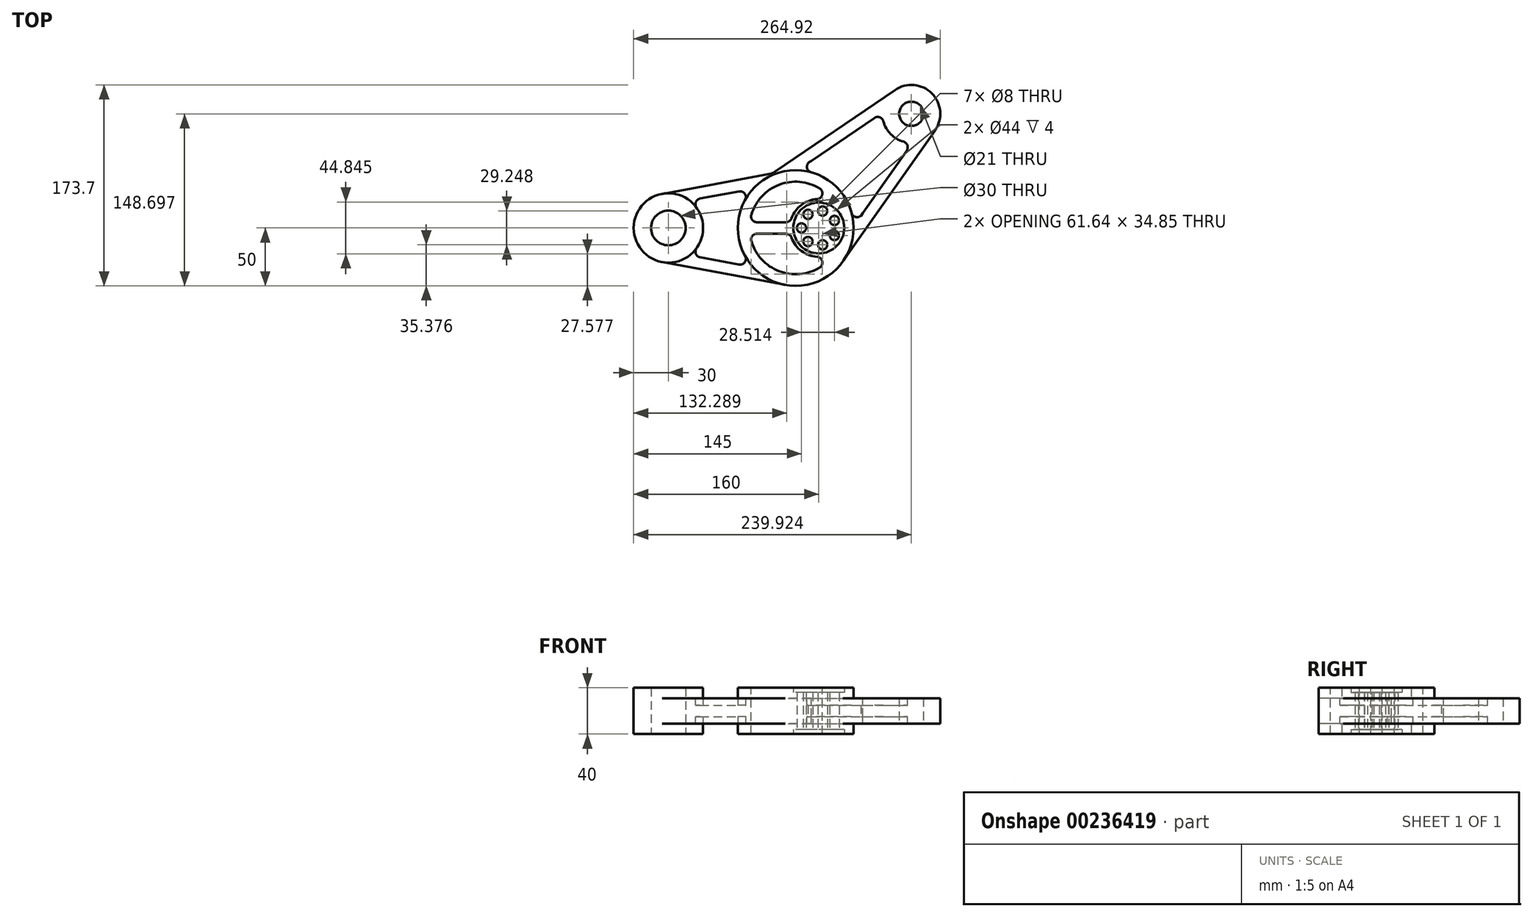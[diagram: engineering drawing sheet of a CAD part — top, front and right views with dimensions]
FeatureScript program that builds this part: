
annotation { "Feature Type Name" : "Feature", "Feature Type Description" : "" }
export const myFeature = defineFeature(function(context is Context, id is Id, definition is map)
    precondition{}
    {
        {
            var Q0;
            Q0=qCreatedBy(makeId("Top.planeOp"),FACE);
            var sketch = newSketch(context, id + "F0", { "sketchPlane" : qUnion([Q0])});
            skCircle(sketch, "E0", {"center": v(0, 0) * mm, "radius": 22 * mm});
            skLineSegment(sketch, "E1", {"start": v(0, 0) * mm, "end": v(111.9, 138.18) * mm, "construction": true});
            skLineSegment(sketch, "E2", {"start": v(0, 0) * mm, "end": v(-200, 0) * mm, "construction": true});
            skLineSegment(sketch, "E3", {"start": v(-135.45, -29.5) * mm, "end": v(-29.1, -49.17) * mm});
            skLineSegment(sketch, "E4.0", {"start": v(-102.54, -25.42) * mm, "end": v(-69, -31.62) * mm});
            skPoint(sketch, "E5.visualSharp", {"position": v(-111.65, -23.73) * mm});
            skArc(sketch, "E5.filletArc", {"start": v(-105.68, -17.57) * mm, "mid": v(-106.27, -22.36) * mm, "end": v(-102.54, -25.42) * mm});
            skPoint(sketch, "E6.visualSharp", {"position": v(-56.77, -33.88) * mm});
            skArc(sketch, "E6.filletArc", {"start": v(-69, -31.62) * mm, "mid": v(-64.02, -29.62) * mm, "end": v(-63.71, -24.28) * mm});
            skPoint(sketch, "E7.visualSharp", {"position": v(-57.08, 33.82) * mm});
            skCircle(sketch, "E8.converted", {"center": v(-130, 0) * mm, "radius": 30 * mm});
            skCircle(sketch, "E9.converted", {"center": v(-20, 0) * mm, "radius": 50 * mm});
            skLineSegment(sketch, "E10", {"start": v(20.9, -28.75) * mm, "end": v(100.38, 84.32) * mm});
            skLineSegment(sketch, "E11.MirrorCS", {"start": v(-37.85, 48.59) * mm, "end": v(65.94, 119.42) * mm});
            skLineSegment(sketch, "E12.MirrorCS", {"start": v(-135.45, 29.5) * mm, "end": v(-42.43, 46.7) * mm});
            skPoint(sketch, "E13.newPointA", {"position": v(-29.1, 49.17) * mm});
            skPoint(sketch, "E13.newPointB", {"position": v(-48.22, 41.51) * mm});
            skArc(sketch, "E13.filletArc", {"start": v(-42.43, 46.7) * mm, "mid": v(-40.04, 47.4) * mm, "end": v(-37.85, 48.59) * mm});
            skArc(sketch, "E14", {"start": v(-102.54, 25.42) * mm, "mid": v(-106.27, 22.36) * mm, "end": v(-105.68, 17.57) * mm});
            skPoint(sketch, "E14.second.point", {"position": v(-105.68, 17.57) * mm});
            skPoint(sketch, "E14.third.point", {"position": v(-97.06, 18.48) * mm});
            skLineSegment(sketch, "E15.trimOffspring", {"start": v(-102.54, 25.42) * mm, "end": v(-69, 31.62) * mm});
            skArc(sketch, "E16", {"start": v(-63.71, 24.28) * mm, "mid": v(-64.02, 29.62) * mm, "end": v(-69, 31.62) * mm});
            skPoint(sketch, "E16.first.point", {"position": v(-63.71, 24.28) * mm});
            skPoint(sketch, "E16.second.point", {"position": v(-69, 31.62) * mm});
            skPoint(sketch, "E16.third.point", {"position": v(-71.92, 23.5) * mm});
            skLineSegment(sketch, "E17.trimOffspring", {"start": v(-57.08, 33.82) * mm, "end": v(-56.77, 33.88) * mm});
            skLineSegment(sketch, "E18.0", {"start": v(36.22, 10.43) * mm, "end": v(75.93, 66.93) * mm});
            skLineSegment(sketch, "E19.0", {"start": v(-18.1, 49.96) * mm, "end": v(-18.1, 49.96) * mm});
            skArc(sketch, "E20", {"start": v(54.93, 99.26) * mm, "mid": v(62.32, 80.95) * mm, "end": v(80.7, 73.7) * mm});
            skArc(sketch, "E21", {"start": v(80.7, 73.7) * mm, "mid": v(97.53, 116.45) * mm, "end": v(54.93, 99.26) * mm});
            skLineSegment(sketch, "E22", {"start": v(-9.3, 55.97) * mm, "end": v(48.1, 95.14) * mm});
            skArc(sketch, "E23", {"start": v(-6.58, 57.82) * mm, "mid": v(-10.28, 53.01) * mm, "end": v(-6.62, 48.18) * mm});
            skPoint(sketch, "E23.first.point", {"position": v(-6.58, 57.82) * mm});
            skPoint(sketch, "E23.second.point", {"position": v(-6.62, 48.18) * mm});
            skPoint(sketch, "E23.third.point", {"position": v(-0.45, 51.7) * mm});
            skArc(sketch, "E24", {"start": v(28.27, 13.03) * mm, "mid": v(32.94, 9.34) * mm, "end": v(37.83, 12.72) * mm});
            skPoint(sketch, "E24.first.point", {"position": v(28.27, 13.03) * mm});
            skPoint(sketch, "E24.second.point", {"position": v(37.83, 12.72) * mm});
            skPoint(sketch, "E24.third.point", {"position": v(35.4, 18.78) * mm});
            skArc(sketch, "E25", {"start": v(55.76, 92.3) * mm, "mid": v(52.67, 95.7) * mm, "end": v(48.1, 95.14) * mm});
            skPoint(sketch, "E25.first.point", {"position": v(48.1, 95.14) * mm});
            skPoint(sketch, "E25.second.point", {"position": v(55.76, 92.3) * mm});
            skPoint(sketch, "E25.third.point", {"position": v(50.2, 86.07) * mm});
            skArc(sketch, "E26", {"start": v(75.93, 66.93) * mm, "mid": v(76.55, 71.49) * mm, "end": v(73.19, 74.62) * mm});
            skPoint(sketch, "E26.first.point", {"position": v(75.93, 66.93) * mm});
            skPoint(sketch, "E26.second.point", {"position": v(73.19, 74.62) * mm});
            skPoint(sketch, "E26.third.point", {"position": v(66.94, 68.8) * mm});
            skCircle(sketch, "E27", {"center": v(-130, 0) * mm, "radius": 15 * mm});
            skCircle(sketch, "E28", {"center": v(79.92, 98.7) * mm, "radius": 10.5 * mm});
            skCircle(sketch, "E29", {"center": v(0, 0) * mm, "radius": 15 * mm, "construction": true});
            skCircle(sketch, "E30", {"center": v(-15, 0) * mm, "radius": 4 * mm});
            skCircle(sketch, "E31.1.0", {"center": v(-9.35, -11.73) * mm, "radius": 4 * mm});
            skCircle(sketch, "E31.2.0", {"center": v(3.34, -14.62) * mm, "radius": 4 * mm});
            skCircle(sketch, "E32.1.3.0", {"center": v(13.51, -6.5) * mm, "radius": 4 * mm});
            skCircle(sketch, "E32.1.4.0", {"center": v(13.51, 6.5) * mm, "radius": 4 * mm});
            skCircle(sketch, "E32.1.5.0", {"center": v(3.34, 14.62) * mm, "radius": 4 * mm});
            skCircle(sketch, "E32.1.6.0", {"center": v(-9.35, 11.73) * mm, "radius": 4 * mm});
            skSolve(sketch);
        }
        {
            var Q0;
            {var subQ4=sQuery(id+"F0.wireOp",EDGE,"E10");Q0=makeQuery(id+"F0.imprint","IMPRINT",FACE,{"disambiguationData":[TD([[makeQuery(id+"F0.imprint","IMPRINT",EDGE,{"derivedFrom":subQ4}),1.0]])]});}
            var Q1;
            {var subQ2=sQuery(id+"F0.wireOp",EDGE,"E3");Q1=makeQuery(id+"F0.imprint","IMPRINT",FACE,{"disambiguationData":[TD([[makeQuery(id+"F0.imprint","IMPRINT",EDGE,{"derivedFrom":subQ2}),1.0]])]});}
            var Q2;
            {var subQ10=sQuery(id+"F0.wireOp",EDGE,"E12.MirrorCS");Q2=makeQuery(id+"F0.imprint","IMPRINT",FACE,{"disambiguationData":[TD([[makeQuery(id+"F0.imprint","IMPRINT",EDGE,{"derivedFrom":subQ10}),-1.0]])]});}
            extrude(context, id + "F1", {"entities" : qUnion([Q0, Q1, Q2]), "endBound" : BoundingType.SYMMETRIC, "oppositeDirection" : true, "depth" : 22 * mm});
        }
        {
            var Q0;
            Q0=makeQuery(id+"F0.imprint","IMPRINT",FACE,{"disambiguationData":[TD([[makeQuery(id+"F0.imprint","IMPRINT",EDGE,{"derivedFrom":sQuery(id+"F0.wireOp",EDGE,"E4.0")}),1.0]])]});
            var Q1;
            {var subQ8=sQuery(id+"F0.wireOp",EDGE,"E25");Q1=makeQuery(id+"F0.imprint","IMPRINT",FACE,{"disambiguationData":[TD([[makeQuery(id+"F0.imprint","IMPRINT",EDGE,{"derivedFrom":subQ8}),1.0]])]});}
            extrude(context, id + "F2", {"entities" : qUnion([Q0, Q1]), "endBound" : BoundingType.SYMMETRIC, "depth" : 10 * mm});
        }
        {
            var Q0;
            Q0=makeQuery(id+"F0.imprint","IMPRINT",FACE,{"disambiguationData":[TD([[makeQuery(id+"F0.imprint","IMPRINT",EDGE,{"derivedFrom":sQuery(id+"F0.wireOp",EDGE,"E28")}),-1.0]])]});
            extrude(context, id + "F3", {"entities" : qUnion([Q0]), "operationType" : NewBodyOperationType.ADD, "endBound" : BoundingType.SYMMETRIC, "depth" : 22 * mm});
        }
        {
            var Q0;
            Q0=makeQuery(id+"F0.imprint","IMPRINT",FACE,{"disambiguationData":[TD([[makeQuery(id+"F0.imprint","IMPRINT",EDGE,{"derivedFrom":sQuery(id+"F0.wireOp",EDGE,"E27")}),-1.0]])]});
            var Q1;
            Q1=makeQuery(id+"F0.imprint","IMPRINT",FACE,{"disambiguationData":[TD([[makeQuery(id+"F0.imprint","IMPRINT",EDGE,{"derivedFrom":sQuery(id+"F0.wireOp",EDGE,"E0")}),-1.0]])]});
            extrude(context, id + "F4", {"entities" : qUnion([Q0, Q1]), "operationType" : NewBodyOperationType.ADD, "endBound" : BoundingType.SYMMETRIC, "depth" : 40 * mm});
        }
        {
            var Q0;
            Q0=makeQuery(id+"F4.opExtrude","CAP_FACE",FACE,{"disambiguationData":[OSD([sQuery(id+"F0.wireOp",EDGE,"E0"),sQuery(id+"F0.wireOp",EDGE,"E9.converted")])],"isStart":false});
            var sketch = newSketch(context, id + "F5", { "sketchPlane" : qUnion([Q0])});
            skCircle(sketch, "E33.0", {"center": v(-20, 0) * mm, "radius": 50 * mm});
            skArc(sketch, "E34", {"start": v(0.71, 34.22) * mm, "mid": v(-34.4, 37.32) * mm, "end": v(-58.33, 11.43) * mm});
            skArc(sketch, "E35", {"start": v(-1.56, 24.95) * mm, "mid": v(-15.06, 19.95) * mm, "end": v(-23.57, 8.33) * mm});
            skLineSegment(sketch, "E36.0", {"start": v(-28.28, -5) * mm, "end": v(-53.54, -5) * mm});
            skLineSegment(sketch, "E37.0", {"start": v(-28.28, 5) * mm, "end": v(-53.54, 5) * mm});
            skArc(sketch, "E38.trimOffspring", {"start": v(-58.33, -11.43) * mm, "mid": v(-34.4, -37.32) * mm, "end": v(0.71, -34.22) * mm});
            skArc(sketch, "E39.trimOffspring", {"start": v(-23.57, -8.33) * mm, "mid": v(-15.06, -19.95) * mm, "end": v(-1.56, -24.95) * mm});
            skArc(sketch, "E40.filletArc", {"start": v(-58.33, 11.43) * mm, "mid": v(-57.55, 7.01) * mm, "end": v(-53.54, 5) * mm});
            skArc(sketch, "E41.filletArc", {"start": v(-53.54, -5) * mm, "mid": v(-57.55, -7.01) * mm, "end": v(-58.33, -11.43) * mm});
            skPoint(sketch, "E42.visualSharp", {"position": v(-24.5, -5) * mm});
            skArc(sketch, "E42.filletArc", {"start": v(-23.57, -8.33) * mm, "mid": v(-25.4, -5.92) * mm, "end": v(-28.28, -5) * mm});
            skPoint(sketch, "E43.visualSharp", {"position": v(14.37, -20.45) * mm});
            skArc(sketch, "E43.filletArc", {"start": v(0.71, -34.22) * mm, "mid": v(2.98, -28.75) * mm, "end": v(-1.56, -24.95) * mm});
            skPoint(sketch, "E44.visualSharp", {"position": v(-24.5, 5) * mm});
            skArc(sketch, "E44.filletArc", {"start": v(-28.28, 5) * mm, "mid": v(-25.4, 5.92) * mm, "end": v(-23.57, 8.33) * mm});
            skPoint(sketch, "E45.visualSharp", {"position": v(14.37, 20.45) * mm});
            skArc(sketch, "E45.filletArc", {"start": v(-1.56, 24.95) * mm, "mid": v(2.98, 28.75) * mm, "end": v(0.71, 34.22) * mm});
            skSolve(sketch);
        }
        {
            var Q0;
            Q0=makeQuery(id+"F5.imprint","IMPRINT",FACE,{"disambiguationData":[TD([[makeQuery(id+"F5.imprint","IMPRINT",EDGE,{"derivedFrom":sQuery(id+"F5.wireOp",EDGE,"E34")}),1.0]])]});
            var Q1;
            Q1=makeQuery(id+"F5.imprint","IMPRINT",FACE,{"disambiguationData":[TD([[makeQuery(id+"F5.imprint","IMPRINT",EDGE,{"derivedFrom":sQuery(id+"F5.wireOp",EDGE,"E36.0")}),1.0]])]});
            extrude(context, id + "F6", {"entities" : qUnion([Q0, Q1]), "operationType" : NewBodyOperationType.REMOVE, "endBound" : BoundingType.THROUGH_ALL, "oppositeDirection" : true, "depth" : 4 * mm});
        }
        {
            var Q0;
            Q0=makeQuery(id+"F0.imprint","IMPRINT",FACE,{"disambiguationData":[TD([[makeQuery(id+"F0.imprint","IMPRINT",EDGE,{"derivedFrom":sQuery(id+"F0.wireOp",EDGE,"E0")}),1.0]])]});
            extrude(context, id + "F7", {"entities" : qUnion([Q0]), "operationType" : NewBodyOperationType.ADD, "endBound" : BoundingType.SYMMETRIC, "depth" : 32 * mm});
        }
    });
